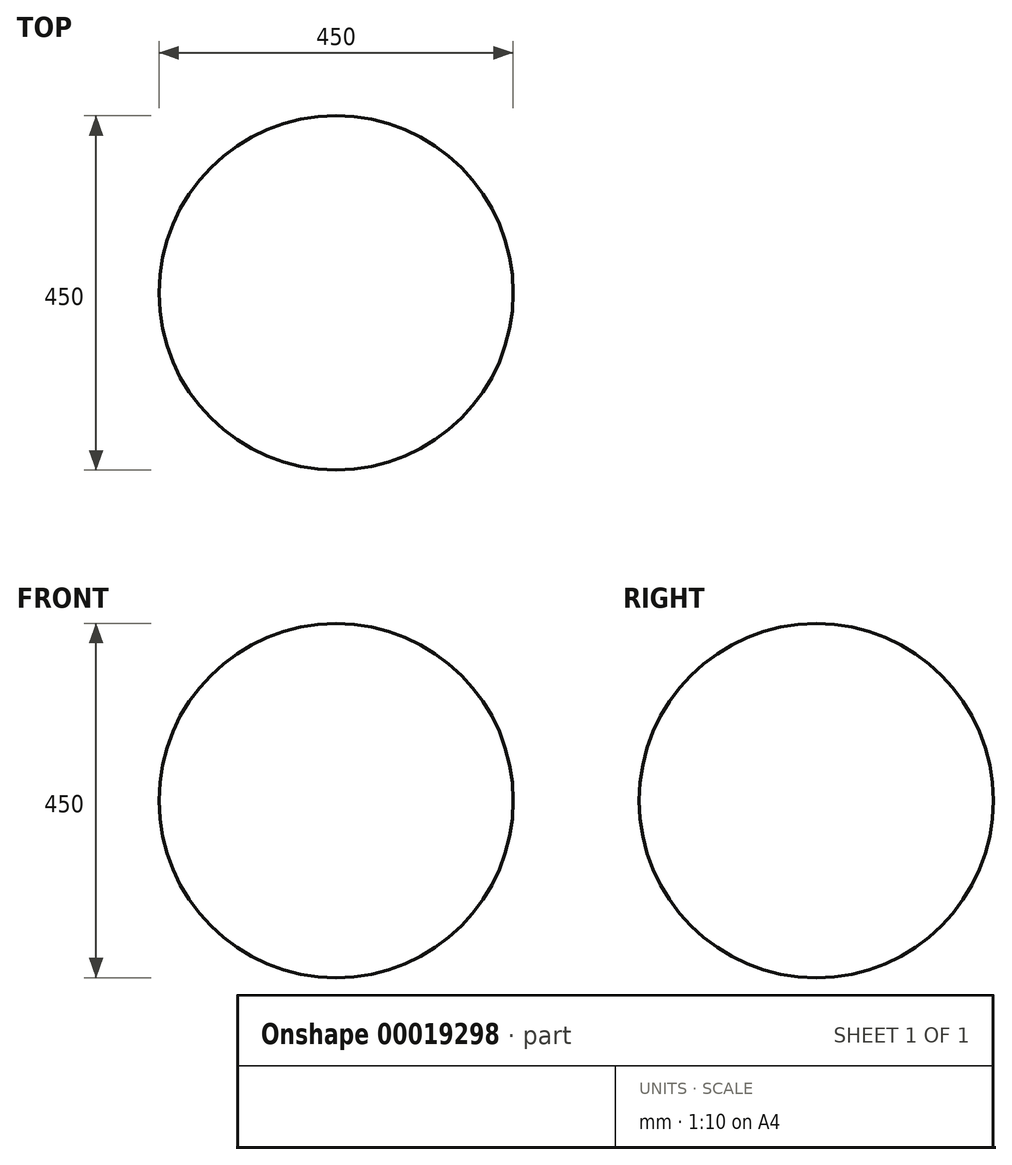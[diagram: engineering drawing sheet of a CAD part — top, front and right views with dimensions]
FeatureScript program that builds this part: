
annotation { "Feature Type Name" : "Feature", "Feature Type Description" : "" }
export const myFeature = defineFeature(function(context is Context, id is Id, definition is map)
    precondition{}
    {
        {
            var Q0;
            Q0=qCreatedBy(makeId("Front.planeOp"),FACE);
            var sketch = newSketch(context, id + "F0", { "sketchPlane" : qUnion([Q0])});
            skArc(sketch, "E0", {"start": v(225, 0) * mm, "mid": v(0, 225) * mm, "end": v(-225, 0) * mm});
            skLineSegment(sketch, "E1", {"start": v(-225, 0) * mm, "end": v(225, 0) * mm});
            skSolve(sketch);
        }
        {
            var Q0;
            Q0=makeQuery(id+"F0.imprint","IMPRINT",FACE,{"disambiguationData":[TD([[makeQuery(id+"F0.imprint","IMPRINT",EDGE,{"derivedFrom":sQuery(id+"F0.wireOp",EDGE,"E0")}),1.0]])]});
            var Q1;
            Q1=sQuery(id+"F0.wireOp",EDGE,"E1");
            revolve(context, id + "F1", {"entities" : qUnion([Q0]), "axis" : qUnion([Q1]), "revolveType" : RevolveType.FULL});
        }
    });
